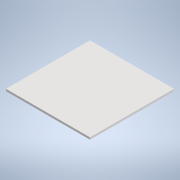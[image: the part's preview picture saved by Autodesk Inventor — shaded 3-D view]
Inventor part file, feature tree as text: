
AUTODESK INVENTOR PART (.ipt)
format: ipt  version: 2022 (Build 260153000, 153)  size: 92,672 bytes
history: native  units: mm
features: other x1, extrude x1, sketch x1
ambient origin geometry x8: Origin, YZ Plane, XZ Plane, XY Plane, X Axis, Y Axis, Z Axis, Center Point
bodies: Body1 (feature_tree)
feature tree (3):
  other  "Твердое тело1"
  extrude  "Выдавливание1"  Depth=250.0mm
  sketch  "Эскиз1"
